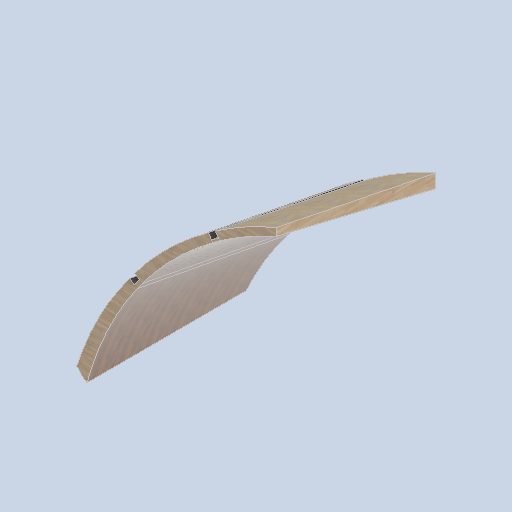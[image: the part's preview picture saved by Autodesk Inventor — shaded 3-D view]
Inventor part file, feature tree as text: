
AUTODESK INVENTOR PART (.ipt)
format: ipt  version: 2024.2 (Build 282272000, 272)  size: 492,032 bytes
history: native  units: mm
features: sketch x12, loft x5, plane x2
ambient origin geometry x8: Origin, YZ Plane, XZ Plane, XY Plane, X Axis, Y Axis, Z Axis, Center Point
bodies: Solid1 (feature_tree)
feature tree (19):
  sketch  "Sketch2"  dims[d3=8500.0mm d4=8500.0mm d5=8500.0mm d6=0.0mm d7=3749.0mm]
  plane  "Work Plane2"
  sketch  "Sketch3"  dims[d8=8500.0mm d9=0.0mm d10=90.0deg]
  loft  "Loft1"
  loft  "Loft2"
  loft  "Loft3"
  loft  "Loft4"
  loft  "Loft5"
  plane  "Work Plane1"
  sketch  "Sketch6"  dims[d11=0.0mm d12=90.0deg d13=8000.0mm]
  sketch  "Sketch7"  dims[d14=0.0mm d15=90.0deg d16=0.0mm d17=90.0deg]
  sketch  "Sketch8"  dims[d18=8500.0mm d19=0.0mm d20=90.0deg]
  sketch  "Sketch9"  dims[d21=0.0mm d22=90.0deg]
  sketch  "Sketch10"  dims[d23=8000.0mm]
  sketch  "Sketch11"  dims[d24=0.0mm d25=90.0deg]
  sketch  "Sketch13"  dims[d26=0.0mm d27=90.0deg]
  sketch  "Sketch14"  dims[d28=8000.0mm]
  sketch  "Sketch15"  dims[d29=8500.0mm]
  sketch  "Sketch18"  dims[d30=0.0mm d31=90.0deg d32=0.0mm d33=90.0deg]
